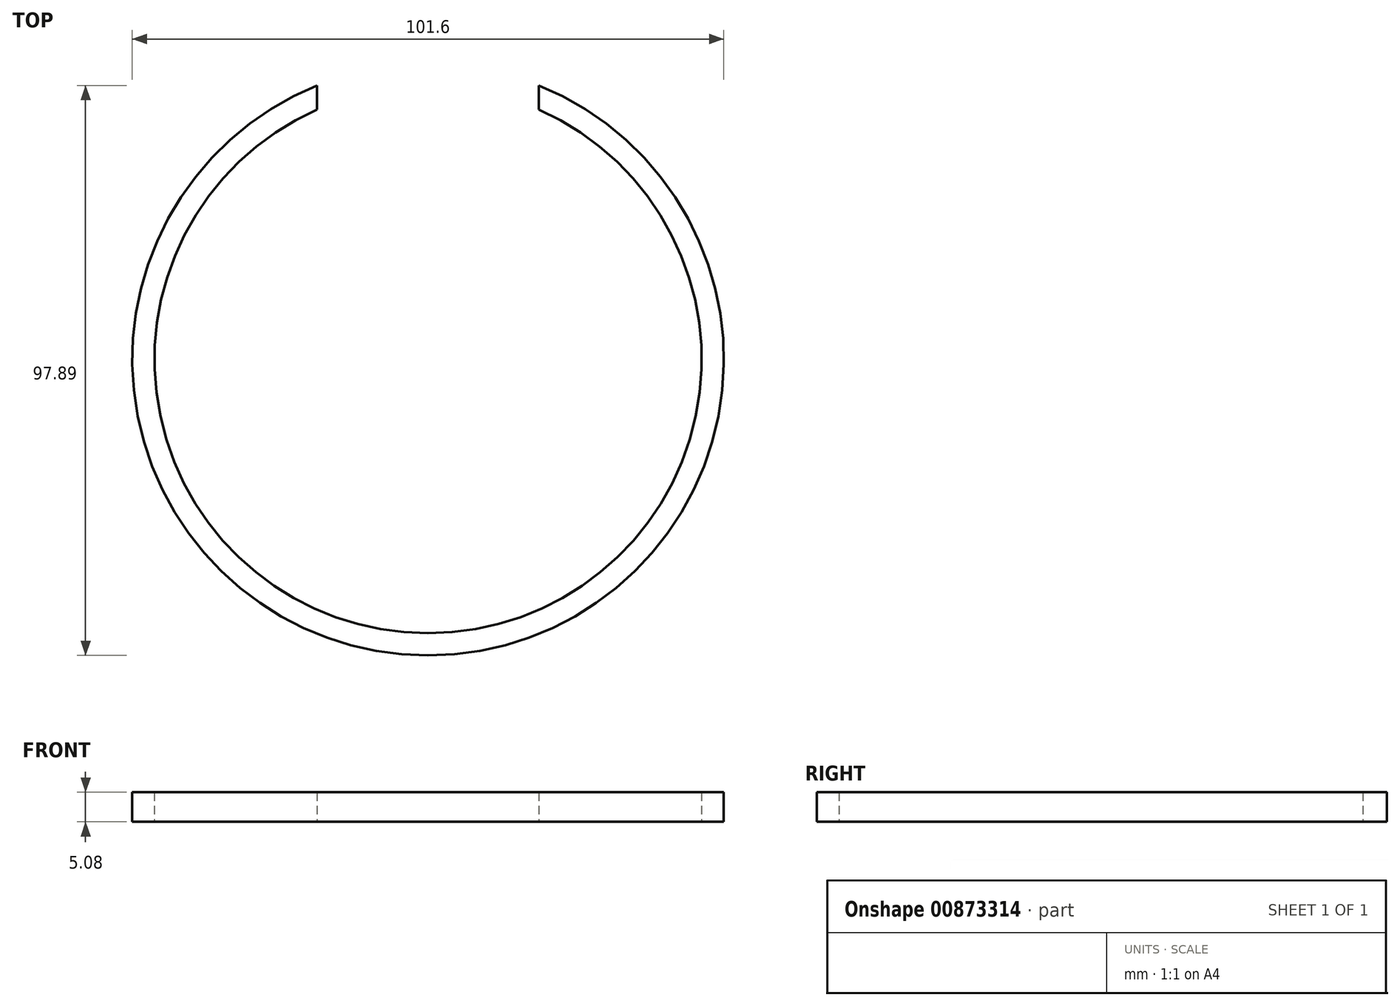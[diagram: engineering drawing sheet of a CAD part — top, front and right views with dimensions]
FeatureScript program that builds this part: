
annotation { "Feature Type Name" : "Feature", "Feature Type Description" : "" }
export const myFeature = defineFeature(function(context is Context, id is Id, definition is map)
    precondition{}
    {
        {
            var Q0;
            Q0=qCreatedBy(makeId("Top.planeOp"),FACE);
            var sketch = newSketch(context, id + "F0", { "sketchPlane" : qUnion([Q0])});
            skArc(sketch, "E0", {"start": v(-19.05, 47.1) * mm, "mid": v(0, -50.8) * mm, "end": v(19.05, 47.1) * mm});
            skLineSegment(sketch, "E1", {"start": v(-19.05, 47.1) * mm, "end": v(0, 47.1) * mm});
            skLineSegment(sketch, "E2", {"start": v(0, 47.1) * mm, "end": v(19.05, 47.1) * mm});
            skArc(sketch, "E3", {"start": v(-19.05, 42.96) * mm, "mid": v(0, -47) * mm, "end": v(19.05, 42.96) * mm});
            skLineSegment(sketch, "E4", {"start": v(-19.05, 42.96) * mm, "end": v(19.05, 42.96) * mm});
            skLineSegment(sketch, "E5", {"start": v(-19.05, 47.1) * mm, "end": v(-19.05, 42.96) * mm});
            skLineSegment(sketch, "E6", {"start": v(19.05, 47.1) * mm, "end": v(19.05, 42.96) * mm});
            skSolve(sketch);
        }
        {
            var Q0;
            Q0=makeQuery(id+"F0.imprint","IMPRINT",FACE,{"disambiguationData":[TD([[makeQuery(id+"F0.imprint","IMPRINT",EDGE,{"derivedFrom":sQuery(id+"F0.wireOp",EDGE,"E0")}),1.0]])]});
            extrude(context, id + "F1", {"entities" : qUnion([Q0]), "depth" : 5.08 * mm, "offsetDistance" : 25.4 * mm});
        }
    });
